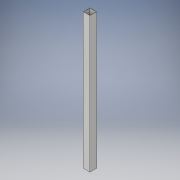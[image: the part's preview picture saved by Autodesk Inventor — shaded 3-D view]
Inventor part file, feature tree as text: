
AUTODESK INVENTOR PART (.ipt)
format: ipt  version: 2018 (Build 220112000, 112)  size: 97,280 bytes
history: native  units: in
note: dims shown in document units (in); Inventor stores cm internally (conversion verified against a paired STEP export)
features: extrude x1, shell x1, sketch x1
ambient origin geometry x8: Origin, YZ Plane, XZ Plane, XY Plane, X Axis, Y Axis, Z Axis, Center Point
bodies: Solid1 (feature_tree)
feature tree (3):
  extrude  "Extrusion1"  Depth=1.0in
  shell  "Shell1"  Thickness=20.0in
  sketch  "Sketch1"  dims[d0=1.0in d1=1.0in d2=20.0in d3=0.0in d4=0.0625in]
